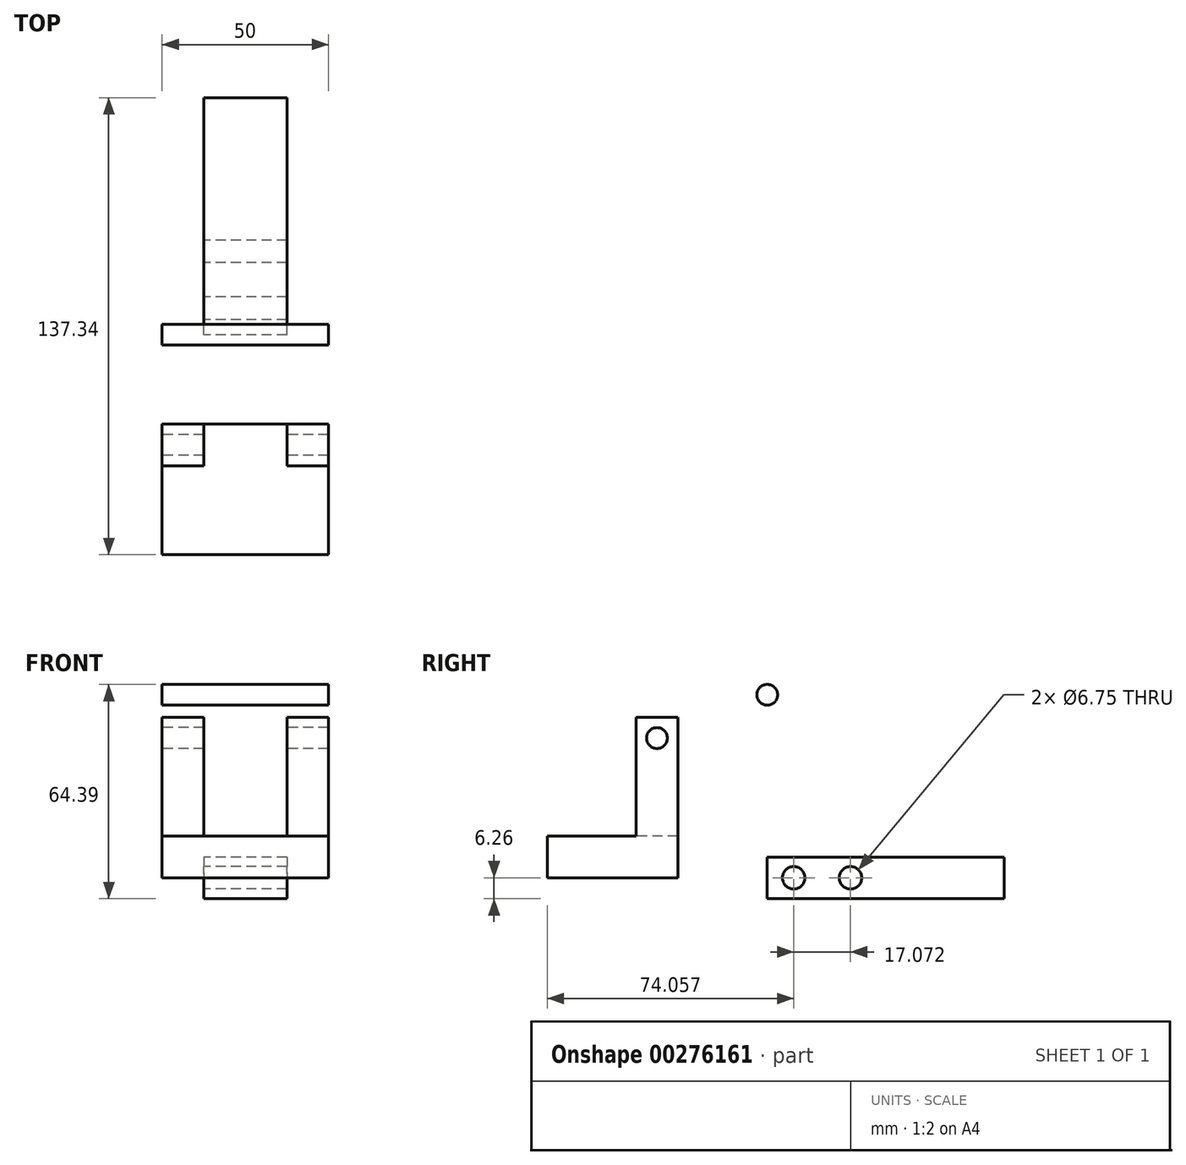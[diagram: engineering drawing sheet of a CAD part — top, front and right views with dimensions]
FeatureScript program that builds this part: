
annotation { "Feature Type Name" : "Feature", "Feature Type Description" : "" }
export const myFeature = defineFeature(function(context is Context, id is Id, definition is map)
    precondition{}
    {
        {
            var Q0;
            Q0=qCreatedBy(makeId("Right.planeOp"),FACE);
            var sketch = newSketch(context, id + "F0", { "sketchPlane" : qUnion([Q0])});
            skLineSegment(sketch, "E0.bottom", {"start": v(0, 6.26) * mm, "end": v(71.25, 6.26) * mm});
            skLineSegment(sketch, "E0.top", {"start": v(0, -6.26) * mm, "end": v(71.25, -6.26) * mm});
            skLineSegment(sketch, "E0.left", {"start": v(0, 6.26) * mm, "end": v(0, -6.26) * mm});
            skLineSegment(sketch, "E0.right", {"start": v(71.25, 6.26) * mm, "end": v(71.25, -6.26) * mm});
            skCircle(sketch, "E1", {"center": v(25.04, 0) * mm, "radius": 3.38 * mm});
            skCircle(sketch, "E2", {"center": v(7.97, 0) * mm, "radius": 3.38 * mm});
            skSolve(sketch);
        }
        {
            var Q0;
            Q0=makeQuery(id+"F0.imprint","IMPRINT",FACE,{"disambiguationData":[TD([[makeQuery(id+"F0.imprint","IMPRINT",EDGE,{"derivedFrom":sQuery(id+"F0.wireOp",EDGE,"E0.bottom")}),-1.0]])]});
            extrude(context, id + "F1", {"entities" : qUnion([Q0]), "endBound" : BoundingType.SYMMETRIC, "depth" : 25 * mm});
        }
        {
            var Q0;
            Q0=qCreatedBy(makeId("Right.planeOp"),FACE);
            var sketch = newSketch(context, id + "F2", { "sketchPlane" : qUnion([Q0])});
            skLineSegment(sketch, "E3", {"start": v(-66.1, 0) * mm, "end": v(-26.88, 0) * mm});
            skLineSegment(sketch, "E4", {"start": v(-26.88, 0) * mm, "end": v(-26.88, 48.28) * mm});
            skLineSegment(sketch, "E5", {"start": v(-26.88, 48.28) * mm, "end": v(-39.4, 48.28) * mm});
            skLineSegment(sketch, "E6", {"start": v(-39.4, 48.28) * mm, "end": v(-39.4, 12.52) * mm});
            skLineSegment(sketch, "E7", {"start": v(-39.4, 12.52) * mm, "end": v(-66.1, 12.52) * mm});
            skLineSegment(sketch, "E8", {"start": v(-66.1, 12.52) * mm, "end": v(-66.1, 0) * mm});
            skCircle(sketch, "E9", {"center": v(-33.14, 42) * mm, "radius": 3.13 * mm});
            skPoint(sketch, "E10", {"position": v(-33.14, 48.28) * mm});
            skSolve(sketch);
        }
        {
            var Q0;
            Q0=makeQuery(id+"F2.imprint","IMPRINT",FACE,{"disambiguationData":[TD([[makeQuery(id+"F2.imprint","IMPRINT",EDGE,{"derivedFrom":sQuery(id+"F2.wireOp",EDGE,"E3")}),1.0]])]});
            extrude(context, id + "F3", {"entities" : qUnion([Q0]), "endBound" : BoundingType.SYMMETRIC, "depth" : 50 * mm});
        }
        {
            var Q0;
            Q0=makeQuery(id+"F3.opExtrude","SWEPT_FACE",FACE,{"disambiguationData":[OSD([sQuery(id+"F2.wireOp",EDGE,"E6")])]});
            var sketch = newSketch(context, id + "F4", { "sketchPlane" : qUnion([Q0])});
            skLineSegment(sketch, "E11.bottom", {"start": v(-12.5, 12.52) * mm, "end": v(12.5, 12.52) * mm});
            skLineSegment(sketch, "E11.top", {"start": v(-12.5, 48.28) * mm, "end": v(12.5, 48.28) * mm});
            skLineSegment(sketch, "E11.left", {"start": v(-12.5, 12.52) * mm, "end": v(-12.5, 48.28) * mm});
            skLineSegment(sketch, "E11.right", {"start": v(12.5, 12.52) * mm, "end": v(12.5, 48.28) * mm});
            skSolve(sketch);
        }
        {
            var Q0;
            Q0 = qSketchRegion(id + "F4", true);
            extrude(context, id + "F5", {"entities" : qUnion([Q0]), "operationType" : NewBodyOperationType.REMOVE, "endBound" : BoundingType.THROUGH_ALL, "oppositeDirection" : true, "depth" : 25 * mm});
        }
        {
            var Q0;
            Q0=qCreatedBy(makeId("Right.planeOp"),FACE);
            var sketch = newSketch(context, id + "F6", { "sketchPlane" : qUnion([Q0])});
            skCircle(sketch, "E12", {"center": v(0, 55) * mm, "radius": 3.13 * mm});
            skSolve(sketch);
        }
        {
            var Q0;
            Q0 = qSketchRegion(id + "F6", true);
            extrude(context, id + "F7", {"entities" : qUnion([Q0]), "endBound" : BoundingType.SYMMETRIC, "depth" : 50 * mm});
        }
    });
